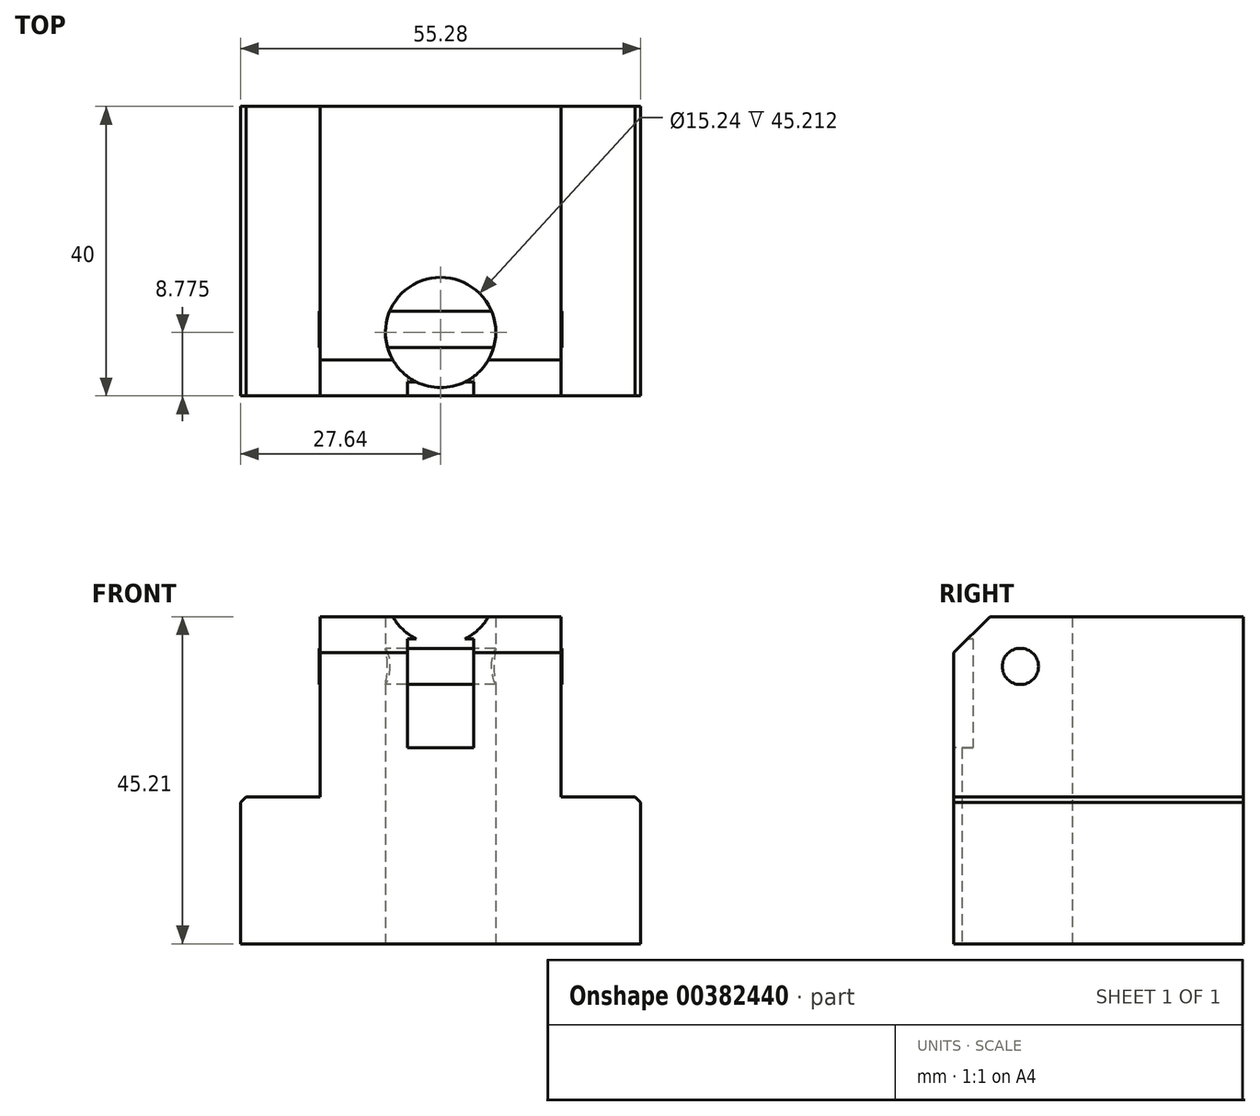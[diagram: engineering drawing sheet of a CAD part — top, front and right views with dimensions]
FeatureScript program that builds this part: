
annotation { "Feature Type Name" : "Feature", "Feature Type Description" : "" }
export const myFeature = defineFeature(function(context is Context, id is Id, definition is map)
    precondition{}
    {
        {
            var Q0;
            Q0=qCreatedBy(makeId("Top.planeOp"),FACE);
            var sketch = newSketch(context, id + "F0", { "sketchPlane" : qUnion([Q0])});
            skLineSegment(sketch, "E0.bottom", {"start": v(-27.64, 20) * mm, "end": v(27.64, 20) * mm});
            skLineSegment(sketch, "E0.top", {"start": v(-27.64, -20) * mm, "end": v(27.64, -20) * mm});
            skLineSegment(sketch, "E0.left", {"start": v(-27.64, 20) * mm, "end": v(-27.64, -20) * mm});
            skLineSegment(sketch, "E0.right", {"start": v(27.64, 20) * mm, "end": v(27.64, -20) * mm});
            skPoint(sketch, "E0.middle", {"position": v(0, 0) * mm});
            skLineSegment(sketch, "E1", {"start": v(-16.64, 20) * mm, "end": v(-16.64, -20) * mm});
            skLineSegment(sketch, "E2", {"start": v(16.64, 20) * mm, "end": v(16.64, -20) * mm});
            skSolve(sketch);
        }
        {
            var Q0;
            {var subQ0=sQuery(id+"F0.wireOp",EDGE,"E1");Q0=makeQuery(id+"F0.imprint","IMPRINT",FACE,{"disambiguationData":[TD([[makeQuery(id+"F0.imprint","IMPRINT",EDGE,{"derivedFrom":subQ0}),1.0]])]});}
            extrude(context, id + "F1", {"entities" : qUnion([Q0]), "depth" : 45.2 * mm});
        }
        {
            var Q0;
            {var subQ0=sQuery(id+"F0.wireOp",EDGE,"E0.left");Q0=makeQuery(id+"F0.imprint","IMPRINT",FACE,{"disambiguationData":[TD([[makeQuery(id+"F0.imprint","IMPRINT",EDGE,{"derivedFrom":subQ0}),1.0]])]});}
            var Q1;
            {var subQ0=sQuery(id+"F0.wireOp",EDGE,"E0.right");Q1=makeQuery(id+"F0.imprint","IMPRINT",FACE,{"disambiguationData":[TD([[makeQuery(id+"F0.imprint","IMPRINT",EDGE,{"derivedFrom":subQ0}),-1.0]])]});}
            extrude(context, id + "F2", {"entities" : qUnion([Q0, Q1]), "operationType" : NewBodyOperationType.ADD, "depth" : 20.32 * mm});
        }
        {
            var Q0;
            Q0=makeQuery(id+"F1.opExtrude","CAP_EDGE",EDGE,{"disambiguationData":[OSD([sQuery(id+"F0.wireOp",EDGE,"E0.top")])],"isStart":false});
            chamfer(context, id + "F3", {"entities" : qUnion([Q0]), "width" : 5 * mm, "tangentPropagation" : true});
        }
        {
            var Q0;
            Q0=qCreatedBy(makeId("Top.planeOp"),FACE);
            var sketch = newSketch(context, id + "F4", { "sketchPlane" : qUnion([Q0])});
            skCircle(sketch, "E3", {"center": v(0, -11.23) * mm, "radius": 7.62 * mm});
            skSolve(sketch);
        }
        {
            var Q0;
            Q0 = qSketchRegion(id + "F4", true);
            extrude(context, id + "F5", {"entities" : qUnion([Q0]), "operationType" : NewBodyOperationType.REMOVE, "depth" : 62.74 * mm});
        }
        {
            var Q0;
            Q0=qCreatedBy(makeId("Right.planeOp"),FACE);
            var sketch = newSketch(context, id + "F6", { "sketchPlane" : qUnion([Q0])});
            skCircle(sketch, "E4", {"center": v(-10.78, 38.33) * mm, "radius": 2.5 * mm});
            skSolve(sketch);
        }
        {
            var Q0;
            Q0 = qSketchRegion(id + "F6", true);
            extrude(context, id + "F7", {"entities" : qUnion([Q0]), "operationType" : NewBodyOperationType.ADD, "endBound" : BoundingType.SYMMETRIC, "depth" : 33.53 * mm});
        }
        {
            var Q0;
            Q0=makeQuery(id+"F2.opExtrude","CAP_EDGE",EDGE,{"disambiguationData":[OSD([sQuery(id+"F0.wireOp",EDGE,"E0.left")])],"isStart":false});
            chamfer(context, id + "F8", {"entities" : qUnion([Q0]), "width" : 0.76 * mm, "tangentPropagation" : true});
        }
        {
            var Q0;
            Q0=makeQuery(id+"F2.opExtrude","CAP_EDGE",EDGE,{"disambiguationData":[OSD([sQuery(id+"F0.wireOp",EDGE,"E0.right")])],"isStart":false});
            chamfer(context, id + "F9", {"entities" : qUnion([Q0]), "width" : 0.76 * mm, "tangentPropagation" : true});
        }
        {
            var Q0;
            {var subQ0=sQuery(id+"F0.wireOp",EDGE,"E0.top");Q0=makeQuery(id+"F2.boolean.opBoolean","MERGE",FACE,{"derivedFrom":[makeQuery(id+"F1.opExtrude","SWEPT_FACE",FACE,{"disambiguationData":[OSD([subQ0])]}),makeQuery(id+"F2.opExtrude","SWEPT_FACE",FACE,{"disambiguationData":[OSD([subQ0]),TDD([makeQuery(id+"F0.imprint","IMPRINT",EDGE,{"disambiguationData":[TD([[makeQuery(id+"F0.imprint","INTERSECT",VERTEX,{"derivedFrom":[subQ0,sQuery(id+"F0.wireOp",EDGE,"E0.left")]}),-1.0]])],"derivedFrom":subQ0})])]}),makeQuery(id+"F2.opExtrude","SWEPT_FACE",FACE,{"disambiguationData":[OSD([subQ0]),TDD([makeQuery(id+"F0.imprint","IMPRINT",EDGE,{"disambiguationData":[TD([[makeQuery(id+"F0.imprint","INTERSECT",VERTEX,{"derivedFrom":[subQ0,sQuery(id+"F0.wireOp",EDGE,"E0.right")]}),1.0]])],"derivedFrom":subQ0})])]})]});}
            var sketch = newSketch(context, id + "F10", { "sketchPlane" : qUnion([Q0])});
            skLineSegment(sketch, "E5.bottom", {"start": v(-4.58, 42.16) * mm, "end": v(4.54, 42.16) * mm});
            skLineSegment(sketch, "E5.top", {"start": v(-4.58, 27.1) * mm, "end": v(4.54, 27.1) * mm});
            skLineSegment(sketch, "E5.left", {"start": v(-4.58, 42.16) * mm, "end": v(-4.58, 27.1) * mm});
            skLineSegment(sketch, "E5.right", {"start": v(4.54, 42.16) * mm, "end": v(4.54, 27.1) * mm});
            skSolve(sketch);
        }
        {
            var Q0;
            Q0 = qSketchRegion(id + "F10", true);
            extrude(context, id + "F11", {"entities" : qUnion([Q0]), "operationType" : NewBodyOperationType.REMOVE, "oppositeDirection" : true, "depth" : 3.05 * mm});
        }
    });
